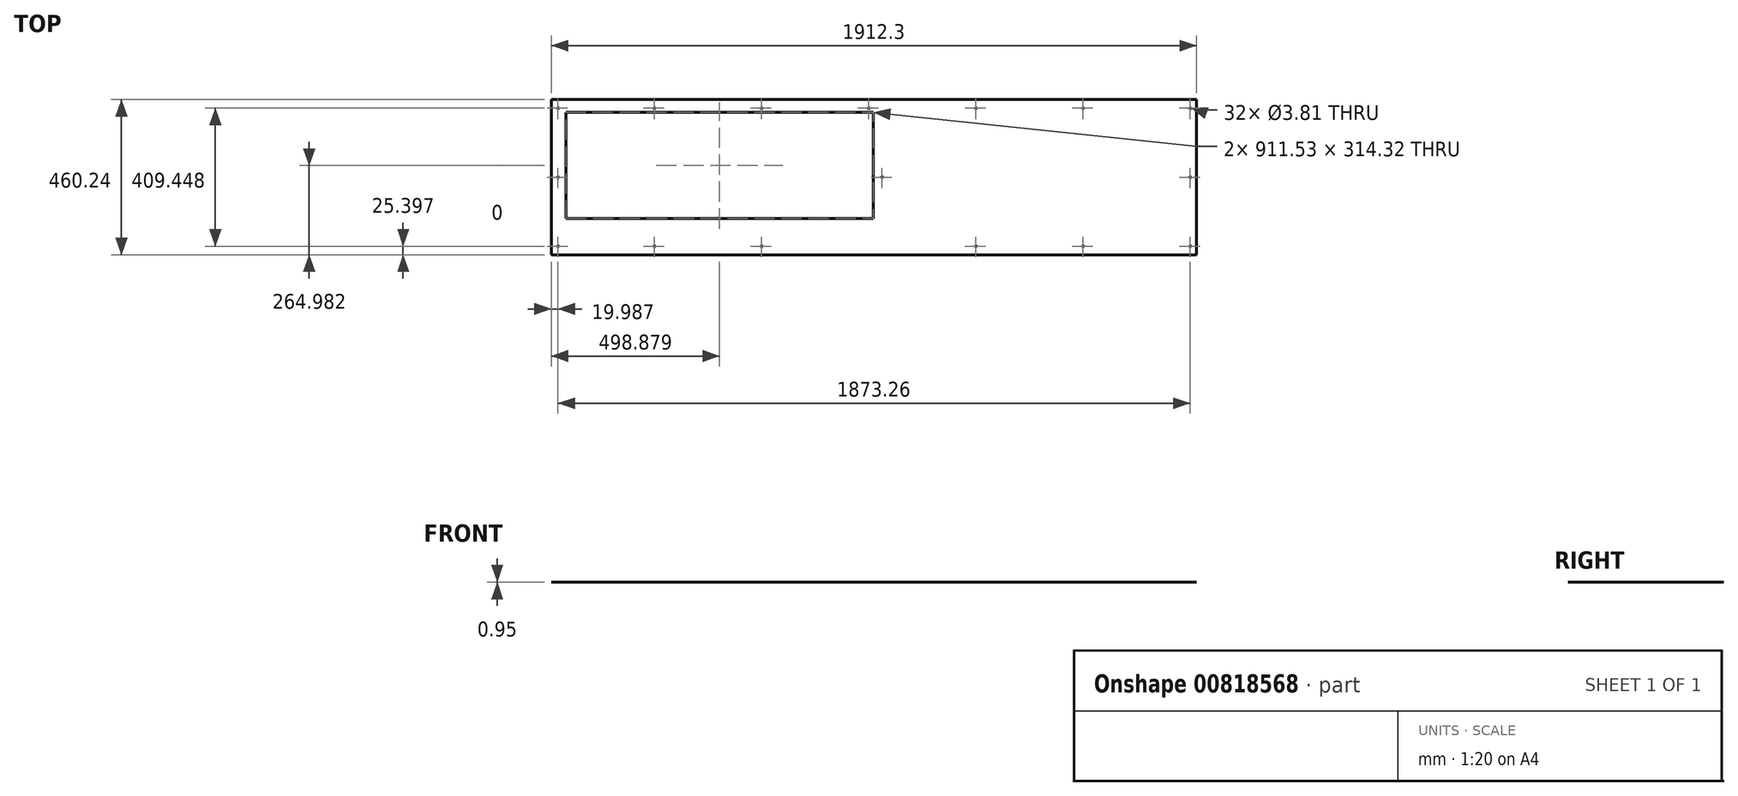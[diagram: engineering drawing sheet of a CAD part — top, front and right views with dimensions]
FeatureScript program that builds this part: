
annotation { "Feature Type Name" : "Feature", "Feature Type Description" : "" }
export const myFeature = defineFeature(function(context is Context, id is Id, definition is map)
    precondition{}
    {
        {
            var Q0;
            Q0=qCreatedBy(makeId("Top.planeOp"),FACE);
            var sketch = newSketch(context, id + "F0", { "sketchPlane" : qUnion([Q0])});
            skLineSegment(sketch, "E0.bottom", {"start": v(-958.66, -28.29) * mm, "end": v(953.64, -28.29) * mm});
            skLineSegment(sketch, "E0.top", {"start": v(-958.66, -488.53) * mm, "end": v(953.64, -488.53) * mm});
            skLineSegment(sketch, "E0.left", {"start": v(-958.66, -28.29) * mm, "end": v(-958.66, -488.53) * mm});
            skLineSegment(sketch, "E0.right", {"start": v(953.64, -28.29) * mm, "end": v(953.64, -488.53) * mm});
            skLineSegment(sketch, "E1.bottom", {"start": v(-915.55, -66.39) * mm, "end": v(-4.02, -66.39) * mm});
            skLineSegment(sketch, "E1.top", {"start": v(-915.55, -380.71) * mm, "end": v(-4.02, -380.71) * mm});
            skLineSegment(sketch, "E1.left", {"start": v(-915.55, -66.39) * mm, "end": v(-915.55, -380.71) * mm});
            skLineSegment(sketch, "E1.right", {"start": v(-4.02, -66.39) * mm, "end": v(-4.02, -380.71) * mm});
            skSolve(sketch);
        }
        {
            var Q0;
            Q0 = qSketchRegion(id + "F0", true);
            extrude(context, id + "F1", {"entities" : qUnion([Q0]), "depth" : 0.95 * mm, "offsetDistance" : 25.4 * mm});
        }
        {
            var Q0;
            Q0=makeQuery(id+"F1.opExtrude","CAP_FACE",FACE,{"disambiguationData":[OSD([sQuery(id+"F0.wireOp",EDGE,"E0.bottom"),sQuery(id+"F0.wireOp",EDGE,"E0.top"),sQuery(id+"F0.wireOp",EDGE,"E0.left"),sQuery(id+"F0.wireOp",EDGE,"E0.right"),sQuery(id+"F0.wireOp",EDGE,"E1.bottom"),sQuery(id+"F0.wireOp",EDGE,"E1.top"),sQuery(id+"F0.wireOp",EDGE,"E1.left"),sQuery(id+"F0.wireOp",EDGE,"E1.right")])],"isStart":true});
            var sketch = newSketch(context, id + "F2", { "sketchPlane" : qUnion([Q0])});
            skCircle(sketch, "E2", {"center": v(934.59, 53.69) * mm, "radius": 1.9 * mm});
            skCircle(sketch, "E3.1.0.0", {"center": v(617.09, 53.69) * mm, "radius": 1.9 * mm});
            skCircle(sketch, "E3.2.0.0", {"center": v(299.59, 53.69) * mm, "radius": 1.9 * mm});
            skCircle(sketch, "E3.3.0.0", {"center": v(-17.91, 53.69) * mm, "radius": 1.9 * mm});
            skCircle(sketch, "E3.4.0.0", {"center": v(-335.41, 53.69) * mm, "radius": 1.9 * mm});
            skCircle(sketch, "E3.5.0.0", {"center": v(-652.91, 53.69) * mm, "radius": 1.9 * mm});
            skLineSegment(sketch, "E3.direction1", {"start": v(934.59, 53.69) * mm, "end": v(617.09, 53.69) * mm, "construction": true});
            skCircle(sketch, "E4", {"center": v(-938.67, 53.69) * mm, "radius": 1.9 * mm});
            skCircle(sketch, "E5", {"center": v(934.59, 258.35) * mm, "radius": 1.9 * mm});
            skCircle(sketch, "E6", {"center": v(934.59, 463.13) * mm, "radius": 1.9 * mm});
            skCircle(sketch, "E7", {"center": v(-938.67, 258.35) * mm, "radius": 1.9 * mm});
            skCircle(sketch, "E8", {"center": v(-938.67, 463.13) * mm, "radius": 1.9 * mm});
            skCircle(sketch, "E9", {"center": v(-652.91, 463.13) * mm, "radius": 1.9 * mm});
            skCircle(sketch, "E10", {"center": v(-335.41, 463.13) * mm, "radius": 1.9 * mm});
            skCircle(sketch, "E11", {"center": v(299.59, 463.13) * mm, "radius": 1.9 * mm});
            skCircle(sketch, "E12", {"center": v(617.09, 463.13) * mm, "radius": 1.9 * mm});
            skCircle(sketch, "E13", {"center": v(21.51, 258.35) * mm, "radius": 1.9 * mm});
            skSolve(sketch);
        }
        {
            var Q0;
            Q0 = qSketchRegion(id + "F2", true);
            extrude(context, id + "F3", {"entities" : qUnion([Q0]), "operationType" : NewBodyOperationType.REMOVE, "oppositeDirection" : true, "depth" : 25.4 * mm, "offsetDistance" : 25.4 * mm});
        }
    });
